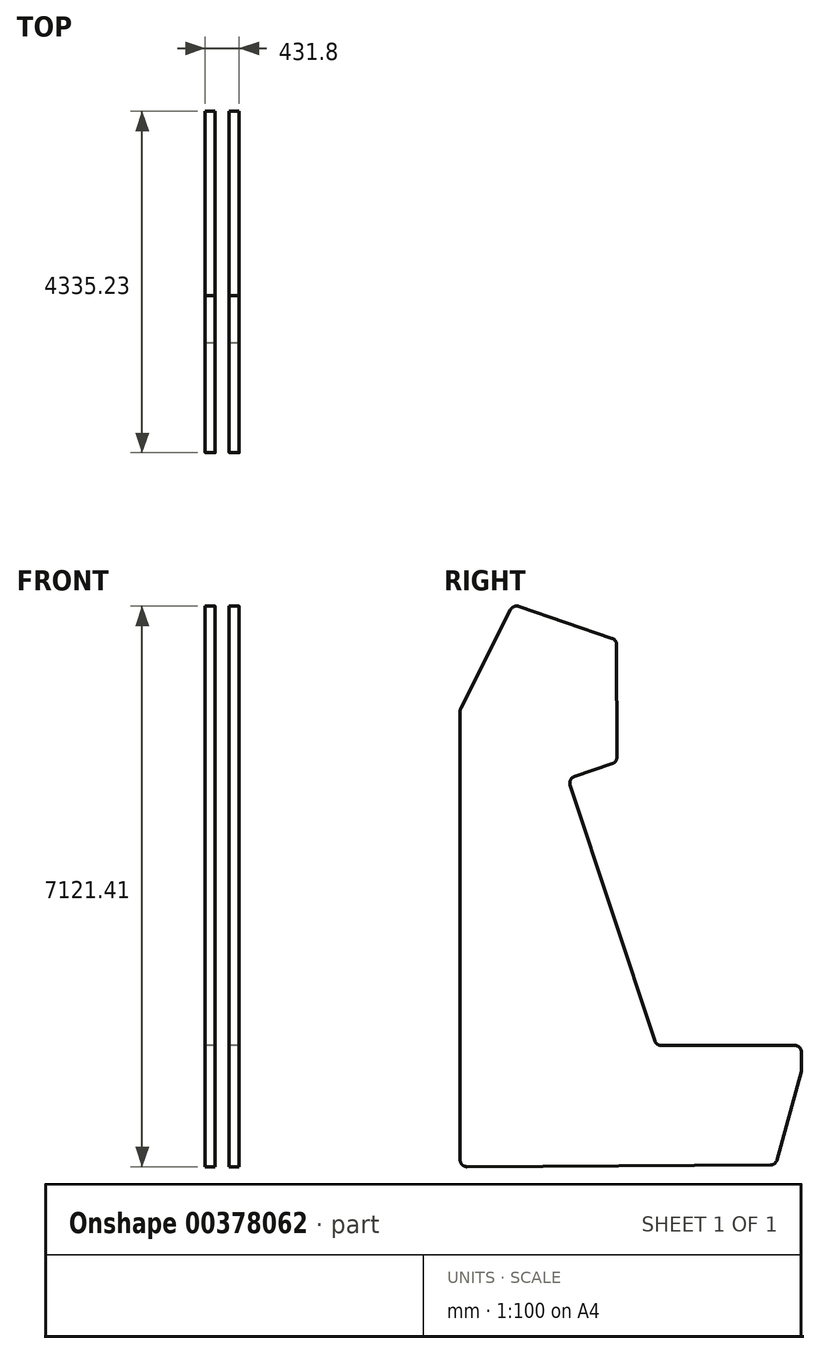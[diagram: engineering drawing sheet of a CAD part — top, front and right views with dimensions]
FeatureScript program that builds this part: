
annotation { "Feature Type Name" : "Feature", "Feature Type Description" : "" }
export const myFeature = defineFeature(function(context is Context, id is Id, definition is map)
    precondition{}
    {
        {
            var Q0;
            Q0=qCreatedBy(makeId("Right.planeOp"),FACE);
            var sketch = newSketch(context, id + "F0", { "sketchPlane" : qUnion([Q0])});
            skArc(sketch, "E0", {"start": v(4490.63, -8958.1) * mm, "mid": v(4620.42, -8913.68) * mm, "end": v(4696.98, -8799.84) * mm});
            skArc(sketch, "E1", {"start": v(-456.13, 7780.87) * mm, "mid": v(-496.51, 7905.63) * mm, "end": v(-601.8, 7983.78) * mm});
            skArc(sketch, "E2", {"start": v(-3601.4, 9007.46) * mm, "mid": v(-3752.08, 9003.1) * mm, "end": v(-3862.91, 8900.92) * mm});
            skArc(sketch, "E3", {"start": v(-5464.48, 5734.1) * mm, "mid": v(-5481.76, 5686.91) * mm, "end": v(-5487.63, 5637) * mm});
            skArc(sketch, "E4", {"start": v(-5487.63, -8794.7) * mm, "mid": v(-5424.2, -8947.26) * mm, "end": v(-5271.31, -9009.88) * mm});
            skArc(sketch, "E5", {"start": v(5479.97, -5945.8) * mm, "mid": v(5485.7, -5917.59) * mm, "end": v(5487.63, -5888.87) * mm});
            skArc(sketch, "E6", {"start": v(5487.63, -5326.1) * mm, "mid": v(5424.6, -5173.95) * mm, "end": v(5272.45, -5110.92) * mm});
            skArc(sketch, "E7", {"start": v(772.14, -4963.32) * mm, "mid": v(850.42, -5070.17) * mm, "end": v(976.44, -5110.92) * mm});
            skArc(sketch, "E8", {"start": v(-1815.12, 3538.21) * mm, "mid": v(-1938.23, 3430.32) * mm, "end": v(-1949.81, 3267.04) * mm});
            skArc(sketch, "E9", {"start": v(-589.3, 3957.3) * mm, "mid": v(-483.65, 4036.07) * mm, "end": v(-443.74, 4161.67) * mm});
            skLineSegment(sketch, "E10", {"start": v(-3601.4, 9007.46) * mm, "end": v(-601.8, 7983.78) * mm});
            skLineSegment(sketch, "E11", {"start": v(-5271.31, -9009.88) * mm, "end": v(4490.63, -8958.1) * mm});
            skLineSegment(sketch, "E12", {"start": v(4696.98, -8799.84) * mm, "end": v(5479.97, -5945.8) * mm});
            skLineSegment(sketch, "E13", {"start": v(5487.63, -5888.87) * mm, "end": v(5487.63, -5326.1) * mm});
            skLineSegment(sketch, "E14", {"start": v(5272.45, -5110.92) * mm, "end": v(976.44, -5110.92) * mm});
            skLineSegment(sketch, "E15", {"start": v(772.14, -4963.32) * mm, "end": v(-1949.81, 3267.04) * mm});
            skLineSegment(sketch, "E16", {"start": v(-1815.12, 3538.21) * mm, "end": v(-589.3, 3957.3) * mm});
            skLineSegment(sketch, "E17", {"start": v(-443.74, 4161.67) * mm, "end": v(-456.13, 7780.87) * mm});
            skLineSegment(sketch, "E18", {"start": v(-3862.91, 8900.92) * mm, "end": v(-5464.48, 5734.1) * mm});
            skLineSegment(sketch, "E19", {"start": v(-5487.63, 5637) * mm, "end": v(-5487.63, -8794.7) * mm});
            skSolve(sketch);
        }
        {
            var Q0;
            Q0 = qSketchRegion(id + "F0", true);
            extrude(context, id + "F1", {"entities" : qUnion([Q0]), "depth" : 321.5 * mm});
        }
        {
            var Q0;
            Q0=makeQuery(id+"F1.opExtrude","SWEPT_BODY",BODY,{"disambiguationData":[OSD([sQuery(id+"F0.wireOp",EDGE,"E0"),sQuery(id+"F0.wireOp",EDGE,"E1"),sQuery(id+"F0.wireOp",EDGE,"E2"),sQuery(id+"F0.wireOp",EDGE,"E3"),sQuery(id+"F0.wireOp",EDGE,"E4"),sQuery(id+"F0.wireOp",EDGE,"E5"),sQuery(id+"F0.wireOp",EDGE,"E6"),sQuery(id+"F0.wireOp",EDGE,"E7"),sQuery(id+"F0.wireOp",EDGE,"E8"),sQuery(id+"F0.wireOp",EDGE,"E9"),sQuery(id+"F0.wireOp",EDGE,"E10"),sQuery(id+"F0.wireOp",EDGE,"E11"),sQuery(id+"F0.wireOp",EDGE,"E12"),sQuery(id+"F0.wireOp",EDGE,"E13"),sQuery(id+"F0.wireOp",EDGE,"E14"),sQuery(id+"F0.wireOp",EDGE,"E15"),sQuery(id+"F0.wireOp",EDGE,"E16"),sQuery(id+"F0.wireOp",EDGE,"E17"),sQuery(id+"F0.wireOp",EDGE,"E18"),sQuery(id+"F0.wireOp",EDGE,"E19")])]});
            var Q1;
            Q1=sQuery(id+"F0.wireOp",VERTEX,"E11.start");
            transform(context, id + "F2", {"entities" : qUnion([Q0]), "transformType" : TransformType.SCALE_UNIFORMLY, "scale" : .395, "scalePoint" : qUnion([Q1]), "makeCopy" : false});
        }
        {
            var Q0;
            Q0=makeQuery(id+"F1.opExtrude","SWEPT_BODY",BODY,{"disambiguationData":[OSD([sQuery(id+"F0.wireOp",EDGE,"E0"),sQuery(id+"F0.wireOp",EDGE,"E1"),sQuery(id+"F0.wireOp",EDGE,"E2"),sQuery(id+"F0.wireOp",EDGE,"E3"),sQuery(id+"F0.wireOp",EDGE,"E4"),sQuery(id+"F0.wireOp",EDGE,"E5"),sQuery(id+"F0.wireOp",EDGE,"E6"),sQuery(id+"F0.wireOp",EDGE,"E7"),sQuery(id+"F0.wireOp",EDGE,"E8"),sQuery(id+"F0.wireOp",EDGE,"E9"),sQuery(id+"F0.wireOp",EDGE,"E10"),sQuery(id+"F0.wireOp",EDGE,"E11"),sQuery(id+"F0.wireOp",EDGE,"E12"),sQuery(id+"F0.wireOp",EDGE,"E13"),sQuery(id+"F0.wireOp",EDGE,"E14"),sQuery(id+"F0.wireOp",EDGE,"E15"),sQuery(id+"F0.wireOp",EDGE,"E16"),sQuery(id+"F0.wireOp",EDGE,"E17"),sQuery(id+"F0.wireOp",EDGE,"E18"),sQuery(id+"F0.wireOp",EDGE,"E19")])]});
            transform(context, id + "F3", {"entities" : qUnion([Q0]), "transformType" : TransformType.TRANSLATION_3D, "dx" : -304.8 * mm, "dy" : 0 * mm, "dz" : 0 * mm, "makeCopy" : true});
        }
    });
